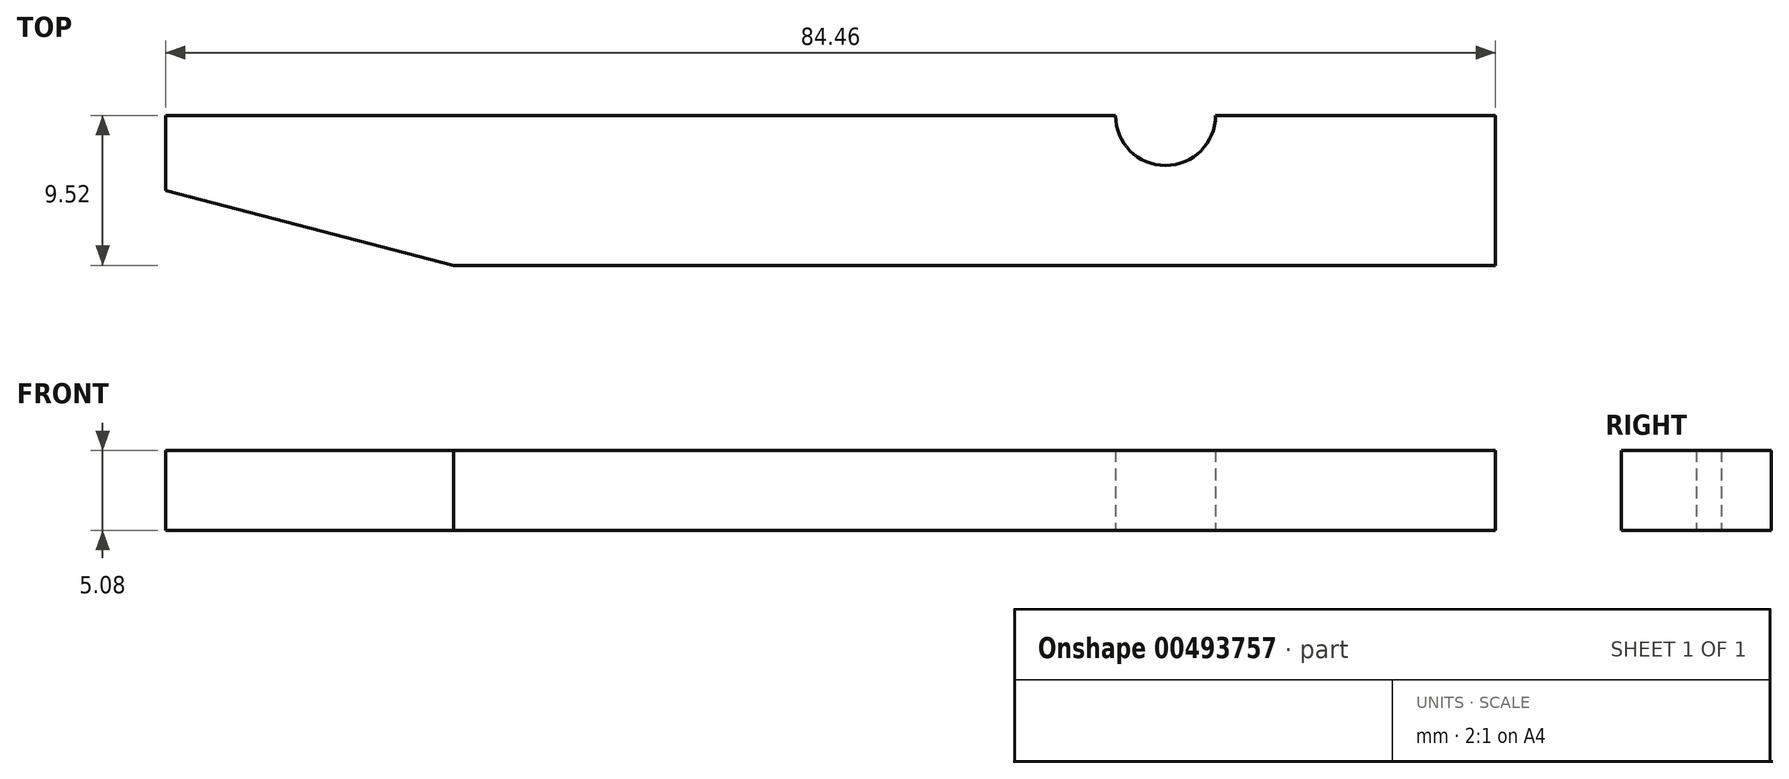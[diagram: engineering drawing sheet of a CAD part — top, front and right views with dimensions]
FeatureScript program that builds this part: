
annotation { "Feature Type Name" : "Feature", "Feature Type Description" : "" }
export const myFeature = defineFeature(function(context is Context, id is Id, definition is map)
    precondition{}
    {
        {
            var Q0;
            Q0=qCreatedBy(makeId("Top.planeOp"),FACE);
            var sketch = newSketch(context, id + "F0", { "sketchPlane" : qUnion([Q0])});
            skLineSegment(sketch, "E0.bottom", {"start": v(-47.37, 4.94) * mm, "end": v(-17.2, 4.94) * mm});
            skLineSegment(sketch, "E0.top", {"start": v(-29.09, -4.58) * mm, "end": v(37.09, -4.58) * mm});
            skLineSegment(sketch, "E0.left", {"start": v(-47.37, 4.94) * mm, "end": v(-47.37, 0.18) * mm});
            skLineSegment(sketch, "E0.right", {"start": v(37.09, 4.94) * mm, "end": v(37.09, -4.58) * mm});
            skLineSegment(sketch, "E1.trimOffspring", {"start": v(19.3, 4.94) * mm, "end": v(37.09, 4.94) * mm});
            skLineSegment(sketch, "E2", {"start": v(-17.2, 4.94) * mm, "end": v(12.96, 4.94) * mm});
            skArc(sketch, "E3", {"start": v(12.96, 4.94) * mm, "mid": v(16.13, 1.77) * mm, "end": v(19.3, 4.94) * mm});
            skLineSegment(sketch, "E4", {"start": v(-47.37, 0.18) * mm, "end": v(-29.09, -4.58) * mm});
            skSolve(sketch);
        }
        {
            var Q0;
            Q0=qSketchRegion(id+"F0",true);
            extrude(context, id + "F1", {"entities" : qUnion([Q0]), "depth" : 5.08 * mm});
        }
    });
